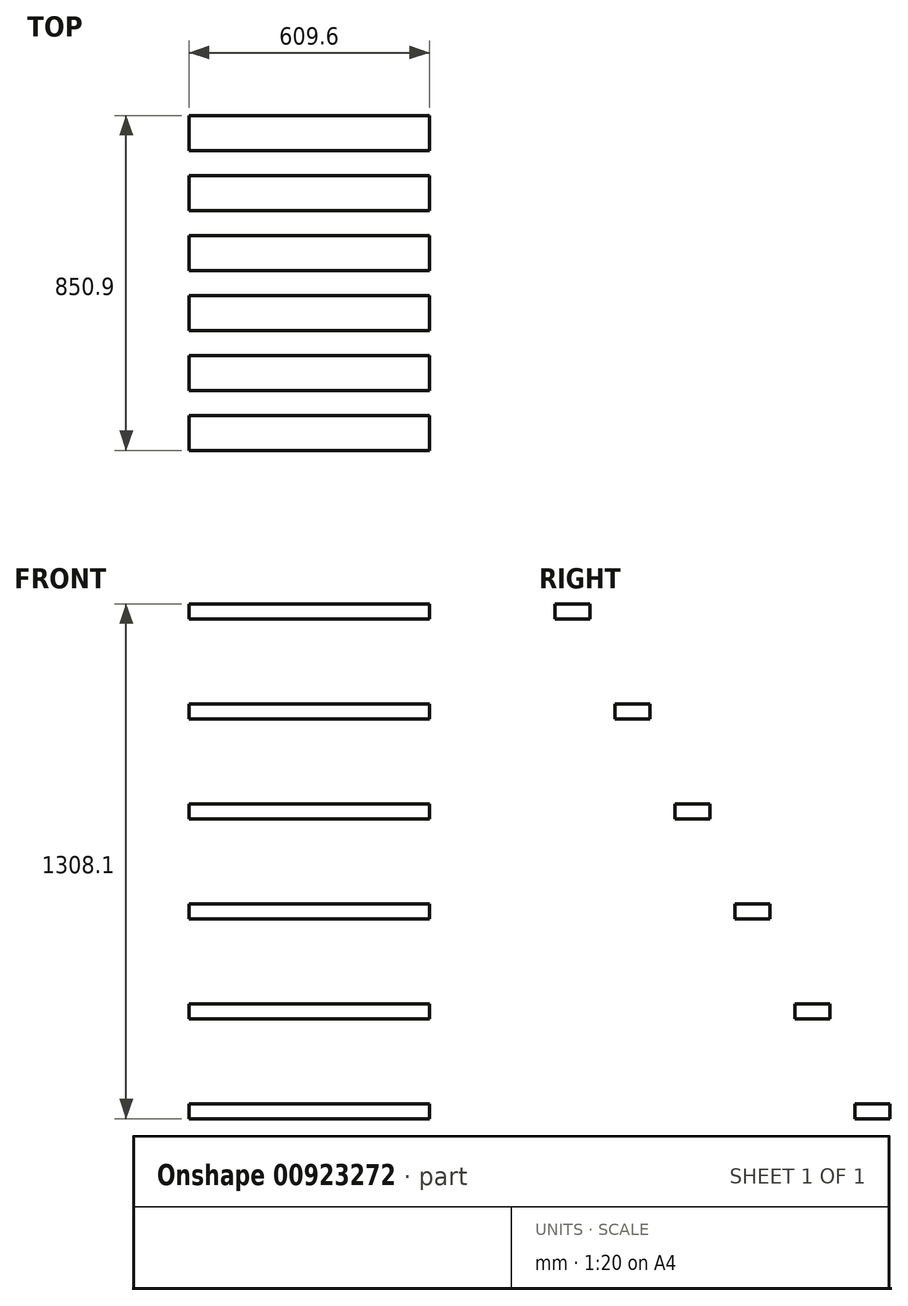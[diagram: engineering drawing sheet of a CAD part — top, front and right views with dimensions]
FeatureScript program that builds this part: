
annotation { "Feature Type Name" : "Feature", "Feature Type Description" : "" }
export const myFeature = defineFeature(function(context is Context, id is Id, definition is map)
    precondition{}
    {
        {
            var Q0;
            Q0=qCreatedBy(makeId("Right.planeOp"),FACE);
            var sketch = newSketch(context, id + "F0", { "sketchPlane" : qUnion([Q0])});
            skPoint(sketch, "E0", {"position": v(0, 254) * mm});
            skPoint(sketch, "E1", {"position": v(-152.4, 254) * mm});
            skLineSegment(sketch, "E2.bottom", {"start": v(-152.4, 254) * mm, "end": v(-63.5, 254) * mm});
            skLineSegment(sketch, "E2.top", {"start": v(-152.4, 292.1) * mm, "end": v(-63.5, 292.1) * mm});
            skLineSegment(sketch, "E2.left", {"start": v(-152.4, 254) * mm, "end": v(-152.4, 292.1) * mm});
            skLineSegment(sketch, "E2.right", {"start": v(-63.5, 254) * mm, "end": v(-63.5, 292.1) * mm});
            skLineSegment(sketch, "E3", {"start": v(0, 0) * mm, "end": v(-152.4, 254) * mm});
            skPoint(sketch, "E4", {"position": v(-152.4, 508) * mm});
            skPoint(sketch, "E5", {"position": v(-304.8, 508) * mm});
            skLineSegment(sketch, "E6.bottom", {"start": v(-304.8, 508) * mm, "end": v(-215.9, 508) * mm});
            skLineSegment(sketch, "E6.top", {"start": v(-304.8, 546.1) * mm, "end": v(-215.9, 546.1) * mm});
            skLineSegment(sketch, "E6.left", {"start": v(-304.8, 508) * mm, "end": v(-304.8, 546.1) * mm});
            skLineSegment(sketch, "E6.right", {"start": v(-215.9, 508) * mm, "end": v(-215.9, 546.1) * mm});
            skPoint(sketch, "E7", {"position": v(-304.8, 762) * mm});
            skPoint(sketch, "E8", {"position": v(-457.2, 762) * mm});
            skLineSegment(sketch, "E9.bottom", {"start": v(-457.2, 762) * mm, "end": v(-368.3, 762) * mm});
            skLineSegment(sketch, "E9.top", {"start": v(-457.2, 800.1) * mm, "end": v(-368.3, 800.1) * mm});
            skLineSegment(sketch, "E9.left", {"start": v(-457.2, 762) * mm, "end": v(-457.2, 800.1) * mm});
            skLineSegment(sketch, "E9.right", {"start": v(-368.3, 762) * mm, "end": v(-368.3, 800.1) * mm});
            skPoint(sketch, "E10", {"position": v(-457.2, 1016) * mm});
            skPoint(sketch, "E11", {"position": v(-609.6, 1016) * mm});
            skLineSegment(sketch, "E12.bottom", {"start": v(-609.6, 1016) * mm, "end": v(-520.7, 1016) * mm});
            skLineSegment(sketch, "E12.top", {"start": v(-609.6, 1054.1) * mm, "end": v(-520.7, 1054.1) * mm});
            skLineSegment(sketch, "E12.left", {"start": v(-609.6, 1016) * mm, "end": v(-609.6, 1054.1) * mm});
            skLineSegment(sketch, "E12.right", {"start": v(-520.7, 1016) * mm, "end": v(-520.7, 1054.1) * mm});
            skPoint(sketch, "E13", {"position": v(-609.6, 1270) * mm});
            skPoint(sketch, "E14", {"position": v(-762, 1270) * mm});
            skLineSegment(sketch, "E15.bottom", {"start": v(-762, 1270) * mm, "end": v(-673.1, 1270) * mm});
            skLineSegment(sketch, "E15.top", {"start": v(-762, 1308.1) * mm, "end": v(-673.1, 1308.1) * mm});
            skLineSegment(sketch, "E15.left", {"start": v(-762, 1270) * mm, "end": v(-762, 1308.1) * mm});
            skLineSegment(sketch, "E15.right", {"start": v(-673.1, 1270) * mm, "end": v(-673.1, 1308.1) * mm});
            skPoint(sketch, "E16", {"position": v(-762, 1524) * mm});
            skPoint(sketch, "E17", {"position": v(-914.4, 1524) * mm});
            skLineSegment(sketch, "E18.bottom", {"start": v(-914.4, 1524) * mm, "end": v(-825.5, 1524) * mm});
            skLineSegment(sketch, "E18.top", {"start": v(-914.4, 1562.1) * mm, "end": v(-825.5, 1562.1) * mm});
            skLineSegment(sketch, "E18.left", {"start": v(-914.4, 1524) * mm, "end": v(-914.4, 1562.1) * mm});
            skLineSegment(sketch, "E18.right", {"start": v(-825.5, 1524) * mm, "end": v(-825.5, 1562.1) * mm});
            skSolve(sketch);
        }
        {
            var Q0;
            Q0 = qSketchRegion(id + "F0", true);
            extrude(context, id + "F1", {"entities" : qUnion([Q0]), "depth" : 609.6 * mm, "offsetDistance" : 25.4 * mm});
        }
    });
